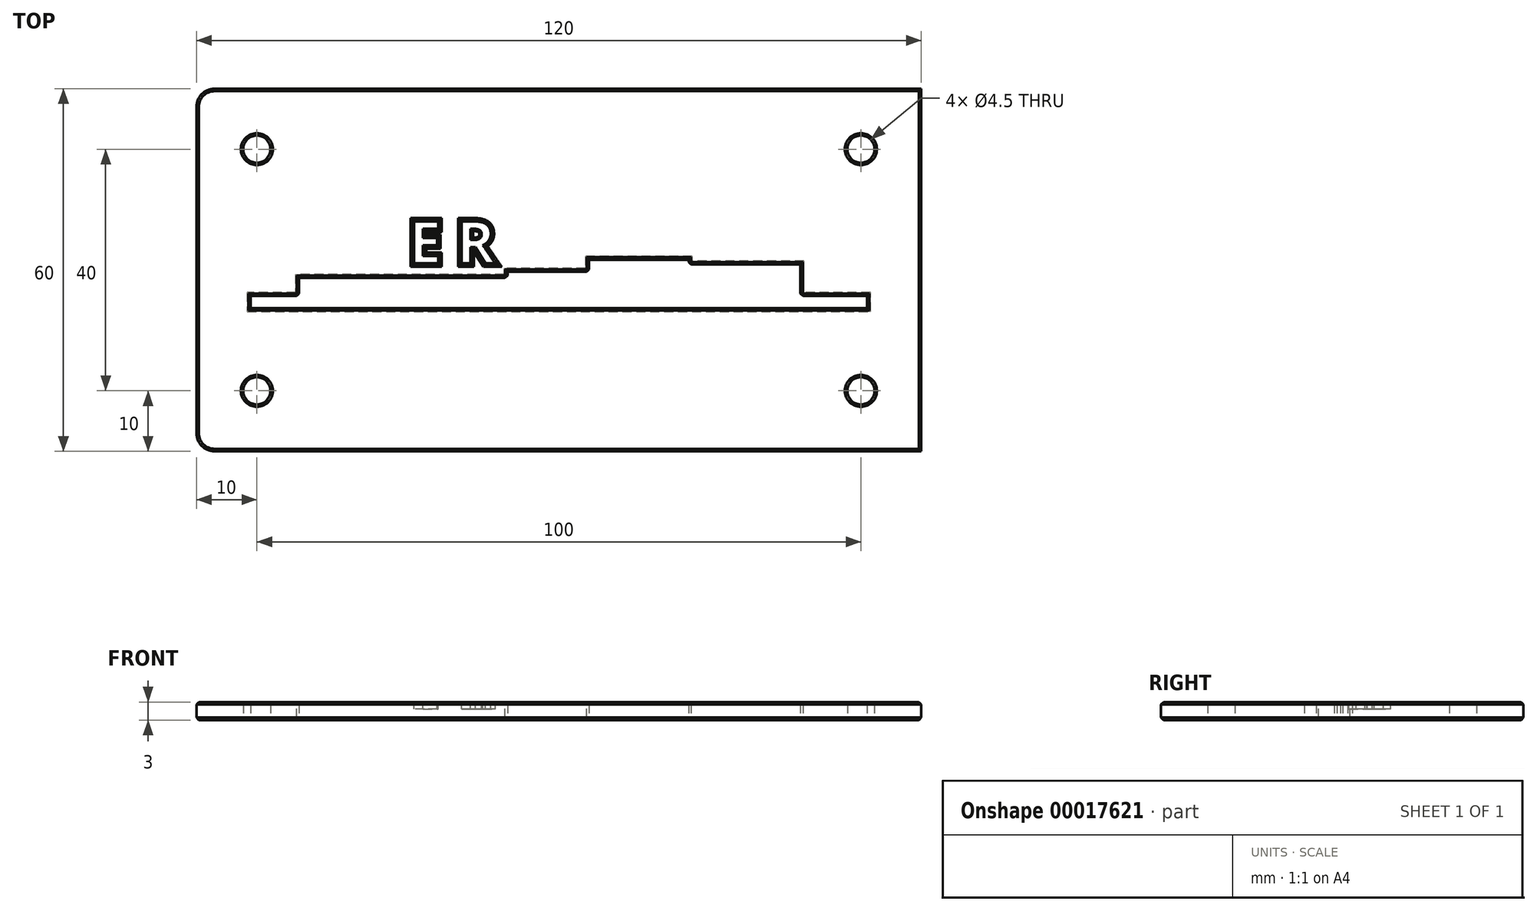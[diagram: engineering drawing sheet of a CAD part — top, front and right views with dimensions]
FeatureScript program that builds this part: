
annotation { "Feature Type Name" : "Feature", "Feature Type Description" : "" }
export const myFeature = defineFeature(function(context is Context, id is Id, definition is map)
    precondition{}
    {
        {
            var Q0;
            Q0=qCreatedBy(makeId("Top.planeOp"),FACE);
            var sketch = newSketch(context, id + "F0", { "sketchPlane" : qUnion([Q0])});
            skLineSegment(sketch, "E0.rect.bottom", {"start": v(-52.5, -30) * mm, "end": v(60, -30) * mm});
            skLineSegment(sketch, "E0.rect.top", {"start": v(-55, 30) * mm, "end": v(60, 30) * mm});
            skLineSegment(sketch, "E0.rect.left", {"start": v(-60, -22.5) * mm, "end": v(-60, 20) * mm});
            skLineSegment(sketch, "E0.rect.right", {"start": v(60, -30) * mm, "end": v(60, 30) * mm});
            skPoint(sketch, "E0.rect.middle", {"position": v(0, 0) * mm});
            skLineSegment(sketch, "E1.left", {"start": v(-60, -30) * mm, "end": v(-60, -22.5) * mm});
            skLineSegment(sketch, "E2.bottom", {"start": v(-60, 30) * mm, "end": v(-55, 30) * mm});
            skLineSegment(sketch, "E2.left", {"start": v(-60, 30) * mm, "end": v(-60, 20) * mm});
            skLineSegment(sketch, "E3.bottom", {"start": v(60, 30) * mm, "end": v(50, 30) * mm});
            skLineSegment(sketch, "E3.left", {"start": v(60, 30) * mm, "end": v(60, 22.5) * mm});
            skLineSegment(sketch, "E4.bottom", {"start": v(60, -30) * mm, "end": v(55, -30) * mm});
            skLineSegment(sketch, "E4.left", {"start": v(60, -30) * mm, "end": v(60, -22.5) * mm});
            skCircle(sketch, "E5", {"center": v(-50, -20) * mm, "radius": 2.25 * mm});
            skCircle(sketch, "E6", {"center": v(-50, 20) * mm, "radius": 2.25 * mm});
            skCircle(sketch, "E7", {"center": v(50, 20) * mm, "radius": 2.25 * mm});
            skCircle(sketch, "E8", {"center": v(50, -20) * mm, "radius": 2.25 * mm});
            skLineSegment(sketch, "E9", {"start": v(-51, 6.3) * mm, "end": v(1.5, 6.3) * mm});
            skLineSegment(sketch, "E10.top", {"start": v(-51, 4.3) * mm, "end": v(-43, 4.3) * mm});
            skLineSegment(sketch, "E10.left", {"start": v(-51, 6.3) * mm, "end": v(-51, 4.3) * mm});
            skLineSegment(sketch, "E10.right", {"start": v(51, 6.3) * mm, "end": v(51, 4.3) * mm});
            skLineSegment(sketch, "E11.top", {"start": v(-43, 1.3) * mm, "end": v(-8.5, 1.3) * mm});
            skLineSegment(sketch, "E11.left", {"start": v(-43, 4.3) * mm, "end": v(-43, 1.3) * mm});
            skLineSegment(sketch, "E12.trimOffspring", {"start": v(43, 4.3) * mm, "end": v(51, 4.3) * mm});
            skLineSegment(sketch, "E13.right", {"start": v(-8.5, 1.3) * mm, "end": v(-8.5, 0.3) * mm});
            skLineSegment(sketch, "E14.left", {"start": v(-8.5, 0.3) * mm, "end": v(-8.5, 1.3) * mm});
            skLineSegment(sketch, "E15.top", {"start": v(-8.5, 0.3) * mm, "end": v(1.5, 0.3) * mm});
            skLineSegment(sketch, "E16", {"start": v(-60, -30) * mm, "end": v(-52.5, -30) * mm});
            skLineSegment(sketch, "E17.right", {"start": v(21.5, 1.3) * mm, "end": v(21.5, 1.6) * mm});
            skLineSegment(sketch, "E18.top", {"start": v(5, -1.7) * mm, "end": v(21.5, -1.7) * mm});
            skLineSegment(sketch, "E18.right", {"start": v(21.5, -0.9) * mm, "end": v(21.5, -1.7) * mm});
            skLineSegment(sketch, "E19.trimOffspring", {"start": v(5, 6.3) * mm, "end": v(21.5, 6.3) * mm});
            skLineSegment(sketch, "E20.trimOffspring", {"start": v(25, 6.3) * mm, "end": v(51, 6.3) * mm});
            skLineSegment(sketch, "E21", {"start": v(-43, 4.3) * mm, "end": v(5, 4.3) * mm, "construction": true});
            skLineSegment(sketch, "E22", {"start": v(1.5, 6.3) * mm, "end": v(5, 6.3) * mm});
            skLineSegment(sketch, "E23", {"start": v(21.5, 6.3) * mm, "end": v(25, 6.3) * mm});
            skLineSegment(sketch, "E24.bottom", {"start": v(43, 4.3) * mm, "end": v(40, 4.3) * mm});
            skLineSegment(sketch, "E24.right", {"start": v(40, 4.3) * mm, "end": v(40, 1.6) * mm});
            skPoint(sketch, "E25.oppositeSnap0", {"position": v(25, 1.6) * mm});
            skPoint(sketch, "E26.orphan", {"position": v(43, -10) * mm});
            skLineSegment(sketch, "E27.trimOffspring", {"start": v(40, 4.3) * mm, "end": v(43, 4.3) * mm, "construction": true});
            skPoint(sketch, "E28.orphan", {"position": v(25, -10.7) * mm});
            skPoint(sketch, "E29.right.start.orphan", {"position": v(25, 13.9) * mm});
            skPoint(sketch, "E30.end.orphan", {"position": v(23, 3.6) * mm});
            skLineSegment(sketch, "E31.top", {"start": v(4.98, 0.3) * mm, "end": v(1.5, 0.3) * mm});
            skLineSegment(sketch, "E32", {"start": v(4.98, 0.3) * mm, "end": v(5, -1.7) * mm});
            skLineSegment(sketch, "E33.top", {"start": v(21.5, -0.9) * mm, "end": v(40, -0.9) * mm});
            skLineSegment(sketch, "E33.right", {"start": v(40, 1.6) * mm, "end": v(40, -0.9) * mm});
            skPoint(sketch, "E34.start.orphan", {"position": v(23, 1.6) * mm});
            skSolve(sketch);
        }
        {
            var Q0;
            Q0=makeQuery(id+"F0.imprint","IMPRINT",FACE,{"disambiguationData":[TD([[makeQuery(id+"F0.imprint","IMPRINT",EDGE,{"derivedFrom":sQuery(id+"F0.wireOp",EDGE,"E0.rect.bottom")}),1.0]])]});
            extrude(context, id + "F1", {"entities" : qUnion([Q0]), "oppositeDirection" : true, "depth" : 3 * mm});
        }
        {
            var Q0;
            Q0=makeQuery(id+"F1.opExtrude","SWEPT_EDGE",EDGE,{"disambiguationData":[OSD([sQuery(id+"F0.wireOp",EDGE,"E4.bottom"),sQuery(id+"F0.wireOp",EDGE,"E4.left")])]});
            var Q1;
            Q1=makeQuery(id+"F1.opExtrude","SWEPT_EDGE",EDGE,{"disambiguationData":[OSD([sQuery(id+"F0.wireOp",EDGE,"E1.bottom"),sQuery(id+"F0.wireOp",EDGE,"E1.left")])]});
            var Q2;
            Q2=makeQuery(id+"F1.opExtrude","SWEPT_EDGE",EDGE,{"disambiguationData":[OSD([sQuery(id+"F0.wireOp",EDGE,"E3.bottom"),sQuery(id+"F0.wireOp",EDGE,"E3.left")])]});
            var Q3;
            Q3=makeQuery(id+"F1.opExtrude","SWEPT_EDGE",EDGE,{"disambiguationData":[OSD([sQuery(id+"F0.wireOp",EDGE,"E2.bottom"),sQuery(id+"F0.wireOp",EDGE,"E2.left")])]});
            fillet(context, id + "F2", {"entities" : qUnion([Q0, Q1, Q2, Q3]), "radius" : 3 * mm, "tangentPropagation" : true, "allowEdgeOverflow" : false});
        }
        {
            var Q0;
            Q0=makeQuery(id+"F1.opExtrude","CAP_FACE",FACE,{"disambiguationData":[OSD([sQuery(id+"F0.wireOp",EDGE,"E0.rect.bottom"),sQuery(id+"F0.wireOp",EDGE,"E0.rect.top"),sQuery(id+"F0.wireOp",EDGE,"E0.rect.left"),sQuery(id+"F0.wireOp",EDGE,"E0.rect.right"),sQuery(id+"F0.wireOp",EDGE,"E1.bottom"),sQuery(id+"F0.wireOp",EDGE,"E1.left"),sQuery(id+"F0.wireOp",EDGE,"E2.bottom"),sQuery(id+"F0.wireOp",EDGE,"E2.left"),sQuery(id+"F0.wireOp",EDGE,"E3.bottom"),sQuery(id+"F0.wireOp",EDGE,"E3.left"),sQuery(id+"F0.wireOp",EDGE,"E4.bottom"),sQuery(id+"F0.wireOp",EDGE,"E4.left"),sQuery(id+"F0.wireOp",EDGE,"E5"),sQuery(id+"F0.wireOp",EDGE,"E6"),sQuery(id+"F0.wireOp",EDGE,"E7"),sQuery(id+"F0.wireOp",EDGE,"E8"),sQuery(id+"F0.wireOp",EDGE,"E9"),sQuery(id+"F0.wireOp",EDGE,"E10.top"),sQuery(id+"F0.wireOp",EDGE,"E10.left"),sQuery(id+"F0.wireOp",EDGE,"E10.right"),sQuery(id+"F0.wireOp",EDGE,"E11.left"),sQuery(id+"F0.wireOp",EDGE,"E11.right"),sQuery(id+"F0.wireOp",EDGE,"E12.trimOffspring"),sQuery(id+"F0.wireOp",EDGE,"E11.top"),sQuery(id+"F0.wireOp",EDGE,"E14.bottom"),sQuery(id+"F0.wireOp",EDGE,"E14.left"),sQuery(id+"F0.wireOp",EDGE,"E14.right"),sQuery(id+"F0.wireOp",EDGE,"2bbd994b-3e8e-4b0d-a158-f2154df3f7ed.trimOffspring"),sQuery(id+"F0.wireOp",EDGE,"E29.top"),sQuery(id+"F0.wireOp",EDGE,"E29.left"),sQuery(id+"F0.wireOp",EDGE,"E29.right")])],"isStart":false});
            var sketch = newSketch(context, id + "F3", { "sketchPlane" : qUnion([Q0])});
            skText(sketch, "E35", { "text": "E", "fontName": "OpenSans-Bold.ttf"});
            skText(sketch, "E36", { "text": "R", "fontName": "OpenSans-Bold.ttf"});
            skPoint(sketch, "E37.right.start.orphan", {"position": v(-26.9, 1.1) * mm});
            skPoint(sketch, "E38.orphan", {"position": v(-8.9, -0.9) * mm});
            skPoint(sketch, "E37.bottom.end.orphan", {"position": v(-26.9, -0.9) * mm});
            skPoint(sketch, "E37.bottom.start.orphan", {"position": v(-17.9, -0.9) * mm});
            skLineSegment(sketch, "E39", {"start": v(-43, -1.3) * mm, "end": v(-8.5, -1.3) * mm});
            const initialGuessF3  = {"E35": [-0.02483, 0.0011, 1, 0, 0.007], "E36": [-0.01696, 0.0011, 1, 0, 0.007]};
            skSetInitialGuess(sketch, initialGuessF3);
            skSolve(sketch);
        }
        {
            var Q0;
            Q0=makeQuery(id+"F3.imprint","IMPRINT",FACE,{"disambiguationData":[TD([[makeQuery(id+"F3.imprint","IMPRINT",EDGE,{"derivedFrom":sQuery(id+"F3.wireOp",EDGE,"E35.sketch_text.stroke-0")}),-1.0]])]});
            var Q1;
            Q1=makeQuery(id+"F3.imprint","IMPRINT",FACE,{"disambiguationData":[TD([[makeQuery(id+"F3.imprint","IMPRINT",EDGE,{"derivedFrom":sQuery(id+"F3.wireOp",EDGE,"E36.sketch_text.stroke-0")}),-1.0]])]});
            extrude(context, id + "F4", {"entities" : qUnion([Q0, Q1]), "operationType" : NewBodyOperationType.REMOVE, "oppositeDirection" : true, "depth" : 1.2 * mm});
        }
        {
            var Q0;
            Q0=makeQuery(id+"F4.boolean.opBoolean","COPY",EDGE,{"derivedFrom":makeQuery(id+"F4.opExtrude","CAP_EDGE",EDGE,{"disambiguationData":[OSD([sQuery(id+"F3.wireOp",EDGE,"E35.sketch_text.stroke-1")])],"isStart":true})});
            var Q1;
            Q1=makeQuery(id+"F4.boolean.opBoolean","COPY",EDGE,{"derivedFrom":makeQuery(id+"F4.opExtrude","CAP_EDGE",EDGE,{"disambiguationData":[OSD([sQuery(id+"F3.wireOp",EDGE,"E35.sketch_text.stroke-2")])],"isStart":true})});
            var Q2;
            Q2=makeQuery(id+"F4.boolean.opBoolean","COPY",EDGE,{"derivedFrom":makeQuery(id+"F4.opExtrude","CAP_EDGE",EDGE,{"disambiguationData":[OSD([sQuery(id+"F3.wireOp",EDGE,"E35.sketch_text.stroke-3")])],"isStart":true})});
            var Q3;
            Q3=makeQuery(id+"F4.boolean.opBoolean","COPY",EDGE,{"derivedFrom":makeQuery(id+"F4.opExtrude","CAP_EDGE",EDGE,{"disambiguationData":[OSD([sQuery(id+"F3.wireOp",EDGE,"E35.sketch_text.stroke-4")])],"isStart":true})});
            var Q4;
            Q4=makeQuery(id+"F4.boolean.opBoolean","COPY",EDGE,{"derivedFrom":makeQuery(id+"F4.opExtrude","CAP_EDGE",EDGE,{"disambiguationData":[OSD([sQuery(id+"F3.wireOp",EDGE,"E35.sketch_text.stroke-5")])],"isStart":true})});
            var Q5;
            Q5=makeQuery(id+"F4.boolean.opBoolean","COPY",EDGE,{"derivedFrom":makeQuery(id+"F4.opExtrude","CAP_EDGE",EDGE,{"disambiguationData":[OSD([sQuery(id+"F3.wireOp",EDGE,"E35.sketch_text.stroke-6")])],"isStart":true})});
            var Q6;
            Q6=makeQuery(id+"F4.boolean.opBoolean","COPY",EDGE,{"derivedFrom":makeQuery(id+"F4.opExtrude","CAP_EDGE",EDGE,{"disambiguationData":[OSD([sQuery(id+"F3.wireOp",EDGE,"E35.sketch_text.stroke-7")])],"isStart":true})});
            var Q7;
            Q7=makeQuery(id+"F4.boolean.opBoolean","COPY",EDGE,{"derivedFrom":makeQuery(id+"F4.opExtrude","CAP_EDGE",EDGE,{"disambiguationData":[OSD([sQuery(id+"F3.wireOp",EDGE,"E35.sketch_text.stroke-8")])],"isStart":true})});
            var Q8;
            Q8=makeQuery(id+"F4.boolean.opBoolean","COPY",EDGE,{"derivedFrom":makeQuery(id+"F4.opExtrude","CAP_EDGE",EDGE,{"disambiguationData":[OSD([sQuery(id+"F3.wireOp",EDGE,"E35.sketch_text.stroke-9")])],"isStart":true})});
            var Q9;
            Q9=makeQuery(id+"F4.boolean.opBoolean","COPY",EDGE,{"derivedFrom":makeQuery(id+"F4.opExtrude","CAP_EDGE",EDGE,{"disambiguationData":[OSD([sQuery(id+"F3.wireOp",EDGE,"E35.sketch_text.stroke-10")])],"isStart":true})});
            var Q10;
            Q10=makeQuery(id+"F4.boolean.opBoolean","COPY",EDGE,{"derivedFrom":makeQuery(id+"F4.opExtrude","CAP_EDGE",EDGE,{"disambiguationData":[OSD([sQuery(id+"F3.wireOp",EDGE,"E35.sketch_text.stroke-11")])],"isStart":true})});
            var Q11;
            Q11=makeQuery(id+"F4.boolean.opBoolean","COPY",EDGE,{"derivedFrom":makeQuery(id+"F4.opExtrude","CAP_EDGE",EDGE,{"disambiguationData":[OSD([sQuery(id+"F3.wireOp",EDGE,"E35.sketch_text.stroke-0")])],"isStart":true})});
            var Q12;
            Q12=makeQuery(id+"F4.boolean.opBoolean","COPY",EDGE,{"derivedFrom":makeQuery(id+"F4.opExtrude","CAP_EDGE",EDGE,{"disambiguationData":[OSD([sQuery(id+"F3.wireOp",EDGE,"E36.sketch_text.stroke-9")])],"isStart":true})});
            var Q13;
            Q13=makeQuery(id+"F4.boolean.opBoolean","COPY",EDGE,{"derivedFrom":makeQuery(id+"F4.opExtrude","CAP_EDGE",EDGE,{"disambiguationData":[OSD([sQuery(id+"F3.wireOp",EDGE,"E36.sketch_text.stroke-8")])],"isStart":true})});
            var Q14;
            Q14=makeQuery(id+"F4.boolean.opBoolean","COPY",EDGE,{"derivedFrom":makeQuery(id+"F4.opExtrude","CAP_EDGE",EDGE,{"disambiguationData":[OSD([sQuery(id+"F3.wireOp",EDGE,"E36.sketch_text.stroke-7")])],"isStart":true})});
            var Q15;
            Q15=makeQuery(id+"F4.boolean.opBoolean","COPY",EDGE,{"derivedFrom":makeQuery(id+"F4.opExtrude","CAP_EDGE",EDGE,{"disambiguationData":[OSD([sQuery(id+"F3.wireOp",EDGE,"E36.sketch_text.stroke-18")])],"isStart":true})});
            var Q16;
            Q16=makeQuery(id+"F4.boolean.opBoolean","COPY",EDGE,{"derivedFrom":makeQuery(id+"F4.opExtrude","CAP_EDGE",EDGE,{"disambiguationData":[OSD([sQuery(id+"F3.wireOp",EDGE,"E36.sketch_text.stroke-17")])],"isStart":true})});
            var Q17;
            Q17=makeQuery(id+"F4.boolean.opBoolean","COPY",EDGE,{"derivedFrom":makeQuery(id+"F4.opExtrude","CAP_EDGE",EDGE,{"disambiguationData":[OSD([sQuery(id+"F3.wireOp",EDGE,"E36.sketch_text.stroke-16")])],"isStart":true})});
            var Q18;
            Q18=makeQuery(id+"F4.boolean.opBoolean","COPY",EDGE,{"derivedFrom":makeQuery(id+"F4.opExtrude","CAP_EDGE",EDGE,{"disambiguationData":[OSD([sQuery(id+"F3.wireOp",EDGE,"E36.sketch_text.stroke-15")])],"isStart":true})});
            var Q19;
            Q19=makeQuery(id+"F4.boolean.opBoolean","COPY",EDGE,{"derivedFrom":makeQuery(id+"F4.opExtrude","CAP_EDGE",EDGE,{"disambiguationData":[OSD([sQuery(id+"F3.wireOp",EDGE,"E36.sketch_text.stroke-14")])],"isStart":true})});
            var Q20;
            Q20=makeQuery(id+"F4.boolean.opBoolean","COPY",EDGE,{"derivedFrom":makeQuery(id+"F4.opExtrude","CAP_EDGE",EDGE,{"disambiguationData":[OSD([sQuery(id+"F3.wireOp",EDGE,"E36.sketch_text.stroke-13")])],"isStart":true})});
            var Q21;
            Q21=makeQuery(id+"F4.boolean.opBoolean","COPY",EDGE,{"derivedFrom":makeQuery(id+"F4.opExtrude","CAP_EDGE",EDGE,{"disambiguationData":[OSD([sQuery(id+"F3.wireOp",EDGE,"E36.sketch_text.stroke-12")])],"isStart":true})});
            var Q22;
            Q22=makeQuery(id+"F4.boolean.opBoolean","COPY",EDGE,{"derivedFrom":makeQuery(id+"F4.opExtrude","CAP_EDGE",EDGE,{"disambiguationData":[OSD([sQuery(id+"F3.wireOp",EDGE,"E36.sketch_text.stroke-11")])],"isStart":true})});
            var Q23;
            Q23=makeQuery(id+"F4.boolean.opBoolean","COPY",EDGE,{"derivedFrom":makeQuery(id+"F4.opExtrude","CAP_EDGE",EDGE,{"disambiguationData":[OSD([sQuery(id+"F3.wireOp",EDGE,"E36.sketch_text.stroke-10")])],"isStart":true})});
            var Q24;
            Q24=makeQuery(id+"F4.boolean.opBoolean","SPLIT",FACE,{"disambiguationData":[TD([makeQuery(id+"F4.opExtrude","SWEPT_FACE",FACE,{"disambiguationData":[OSD([sQuery(id+"F3.wireOp",EDGE,"E36.sketch_text.stroke-0")])]})])],"derivedFrom":makeQuery(id+"F1.opExtrude","CAP_FACE",FACE,{"disambiguationData":[OSD([sQuery(id+"F0.wireOp",EDGE,"E0.rect.bottom"),sQuery(id+"F0.wireOp",EDGE,"E0.rect.top"),sQuery(id+"F0.wireOp",EDGE,"E0.rect.left"),sQuery(id+"F0.wireOp",EDGE,"E0.rect.right"),sQuery(id+"F0.wireOp",EDGE,"E1.left"),sQuery(id+"F0.wireOp",EDGE,"E2.bottom"),sQuery(id+"F0.wireOp",EDGE,"E2.left"),sQuery(id+"F0.wireOp",EDGE,"E3.bottom"),sQuery(id+"F0.wireOp",EDGE,"E3.left"),sQuery(id+"F0.wireOp",EDGE,"E4.bottom"),sQuery(id+"F0.wireOp",EDGE,"E4.left"),sQuery(id+"F0.wireOp",EDGE,"E5"),sQuery(id+"F0.wireOp",EDGE,"E6"),sQuery(id+"F0.wireOp",EDGE,"E7"),sQuery(id+"F0.wireOp",EDGE,"E8"),sQuery(id+"F0.wireOp",EDGE,"E9"),sQuery(id+"F0.wireOp",EDGE,"E10.top"),sQuery(id+"F0.wireOp",EDGE,"E10.left"),sQuery(id+"F0.wireOp",EDGE,"E10.right"),sQuery(id+"F0.wireOp",EDGE,"E11.left"),sQuery(id+"F0.wireOp",EDGE,"E11.right"),sQuery(id+"F0.wireOp",EDGE,"E12.trimOffspring"),sQuery(id+"F0.wireOp",EDGE,"E11.top"),sQuery(id+"F0.wireOp",EDGE,"E29.top"),sQuery(id+"F0.wireOp",EDGE,"E29.left"),sQuery(id+"F0.wireOp",EDGE,"E29.right"),sQuery(id+"F0.wireOp",EDGE,"E15.top"),sQuery(id+"F0.wireOp",EDGE,"E13.right"),sQuery(id+"F0.wireOp",EDGE,"E15.right"),sQuery(id+"F0.wireOp",EDGE,"E16"),sQuery(id+"F0.wireOp",EDGE,"E17.left"),sQuery(id+"F0.wireOp",EDGE,"E17.right"),sQuery(id+"F0.wireOp",EDGE,"b61ca566-ba07-4bff-9836-ffdb72489c4c.left"),sQuery(id+"F0.wireOp",EDGE,"b61ca566-ba07-4bff-9836-ffdb72489c4c.right"),sQuery(id+"F0.wireOp",EDGE,"E18.top"),sQuery(id+"F0.wireOp",EDGE,"E18.left"),sQuery(id+"F0.wireOp",EDGE,"E18.right"),sQuery(id+"F0.wireOp",EDGE,"E19.trimOffspring"),sQuery(id+"F0.wireOp",EDGE,"E20.trimOffspring"),sQuery(id+"F0.wireOp",EDGE,"54661143-fa5e-42c1-9d10-70f3552f3fbd"),sQuery(id+"F0.wireOp",EDGE,"E30"),sQuery(id+"F0.wireOp",EDGE,"E22"),sQuery(id+"F0.wireOp",EDGE,"E23")])],"isStart":false})});
            chamfer(context, id + "F5", {"entities" : qUnion([Q0, Q1, Q2, Q3, Q4, Q5, Q6, Q7, Q8, Q9, Q10, Q11, Q12, Q13, Q14, Q15, Q16, Q17, Q18, Q19, Q20, Q21, Q22, Q23, Q24]), "width" : .4 * mm});
        }
        {
            var Q0;
            Q0=makeQuery(id+"F1.opExtrude","CAP_EDGE",EDGE,{"disambiguationData":[OSD([sQuery(id+"F0.wireOp",EDGE,"E0.rect.bottom"),sQuery(id+"F0.wireOp",EDGE,"E4.bottom"),sQuery(id+"F0.wireOp",EDGE,"E16")])],"isStart":false});
            var Q1;
            {var subQ0=sQuery(id+"F0.wireOp",EDGE,"E1.left");var subQ1=sQuery(id+"F0.wireOp",EDGE,"E16");Q1=makeQuery(id+"F2.opFillet","BLEND_EDGE",EDGE,{"blendedFrom":[makeQuery(id+"F1.opExtrude","SWEPT_EDGE",EDGE,{"disambiguationData":[OSD([subQ0,subQ1])]}),makeQuery(id+"F1.opExtrude","CAP_FACE",FACE,{"disambiguationData":[OSD([sQuery(id+"F0.wireOp",EDGE,"E0.rect.bottom"),sQuery(id+"F0.wireOp",EDGE,"E0.rect.top"),sQuery(id+"F0.wireOp",EDGE,"E0.rect.left"),sQuery(id+"F0.wireOp",EDGE,"E0.rect.right"),subQ0,sQuery(id+"F0.wireOp",EDGE,"E2.bottom"),sQuery(id+"F0.wireOp",EDGE,"E2.left"),sQuery(id+"F0.wireOp",EDGE,"E3.bottom"),sQuery(id+"F0.wireOp",EDGE,"E3.left"),sQuery(id+"F0.wireOp",EDGE,"E4.bottom"),sQuery(id+"F0.wireOp",EDGE,"E4.left"),sQuery(id+"F0.wireOp",EDGE,"E5"),sQuery(id+"F0.wireOp",EDGE,"E6"),sQuery(id+"F0.wireOp",EDGE,"E7"),sQuery(id+"F0.wireOp",EDGE,"E8"),sQuery(id+"F0.wireOp",EDGE,"E9"),sQuery(id+"F0.wireOp",EDGE,"E10.top"),sQuery(id+"F0.wireOp",EDGE,"E10.left"),sQuery(id+"F0.wireOp",EDGE,"E10.right"),sQuery(id+"F0.wireOp",EDGE,"E11.left"),sQuery(id+"F0.wireOp",EDGE,"E11.right"),sQuery(id+"F0.wireOp",EDGE,"E12.trimOffspring"),sQuery(id+"F0.wireOp",EDGE,"E11.top"),sQuery(id+"F0.wireOp",EDGE,"E29.top"),sQuery(id+"F0.wireOp",EDGE,"E29.left"),sQuery(id+"F0.wireOp",EDGE,"E29.right"),sQuery(id+"F0.wireOp",EDGE,"E15.top"),sQuery(id+"F0.wireOp",EDGE,"E13.right"),sQuery(id+"F0.wireOp",EDGE,"E15.right"),subQ1,sQuery(id+"F0.wireOp",EDGE,"E17.left"),sQuery(id+"F0.wireOp",EDGE,"E17.right"),sQuery(id+"F0.wireOp",EDGE,"b61ca566-ba07-4bff-9836-ffdb72489c4c.left"),sQuery(id+"F0.wireOp",EDGE,"b61ca566-ba07-4bff-9836-ffdb72489c4c.right"),sQuery(id+"F0.wireOp",EDGE,"E18.top"),sQuery(id+"F0.wireOp",EDGE,"E18.left"),sQuery(id+"F0.wireOp",EDGE,"E18.right"),sQuery(id+"F0.wireOp",EDGE,"E19.trimOffspring"),sQuery(id+"F0.wireOp",EDGE,"E20.trimOffspring"),sQuery(id+"F0.wireOp",EDGE,"54661143-fa5e-42c1-9d10-70f3552f3fbd"),sQuery(id+"F0.wireOp",EDGE,"E30"),sQuery(id+"F0.wireOp",EDGE,"E22"),sQuery(id+"F0.wireOp",EDGE,"E23")])],"isStart":false})],"blendedInto":[makeQuery(id+"F1.opExtrude","CAP_FACE",FACE,{"disambiguationData":[OSD([sQuery(id+"F0.wireOp",EDGE,"E0.rect.bottom"),sQuery(id+"F0.wireOp",EDGE,"E0.rect.top"),sQuery(id+"F0.wireOp",EDGE,"E0.rect.left"),sQuery(id+"F0.wireOp",EDGE,"E0.rect.right"),subQ0,sQuery(id+"F0.wireOp",EDGE,"E2.bottom"),sQuery(id+"F0.wireOp",EDGE,"E2.left"),sQuery(id+"F0.wireOp",EDGE,"E3.bottom"),sQuery(id+"F0.wireOp",EDGE,"E3.left"),sQuery(id+"F0.wireOp",EDGE,"E4.bottom"),sQuery(id+"F0.wireOp",EDGE,"E4.left"),sQuery(id+"F0.wireOp",EDGE,"E5"),sQuery(id+"F0.wireOp",EDGE,"E6"),sQuery(id+"F0.wireOp",EDGE,"E7"),sQuery(id+"F0.wireOp",EDGE,"E8"),sQuery(id+"F0.wireOp",EDGE,"E9"),sQuery(id+"F0.wireOp",EDGE,"E10.top"),sQuery(id+"F0.wireOp",EDGE,"E10.left"),sQuery(id+"F0.wireOp",EDGE,"E10.right"),sQuery(id+"F0.wireOp",EDGE,"E11.left"),sQuery(id+"F0.wireOp",EDGE,"E11.right"),sQuery(id+"F0.wireOp",EDGE,"E12.trimOffspring"),sQuery(id+"F0.wireOp",EDGE,"E11.top"),sQuery(id+"F0.wireOp",EDGE,"E29.top"),sQuery(id+"F0.wireOp",EDGE,"E29.left"),sQuery(id+"F0.wireOp",EDGE,"E29.right"),sQuery(id+"F0.wireOp",EDGE,"E15.top"),sQuery(id+"F0.wireOp",EDGE,"E13.right"),sQuery(id+"F0.wireOp",EDGE,"E15.right"),subQ1,sQuery(id+"F0.wireOp",EDGE,"E17.left"),sQuery(id+"F0.wireOp",EDGE,"E17.right"),sQuery(id+"F0.wireOp",EDGE,"b61ca566-ba07-4bff-9836-ffdb72489c4c.left"),sQuery(id+"F0.wireOp",EDGE,"b61ca566-ba07-4bff-9836-ffdb72489c4c.right"),sQuery(id+"F0.wireOp",EDGE,"E18.top"),sQuery(id+"F0.wireOp",EDGE,"E18.left"),sQuery(id+"F0.wireOp",EDGE,"E18.right"),sQuery(id+"F0.wireOp",EDGE,"E19.trimOffspring"),sQuery(id+"F0.wireOp",EDGE,"E20.trimOffspring"),sQuery(id+"F0.wireOp",EDGE,"54661143-fa5e-42c1-9d10-70f3552f3fbd"),sQuery(id+"F0.wireOp",EDGE,"E30"),sQuery(id+"F0.wireOp",EDGE,"E22"),sQuery(id+"F0.wireOp",EDGE,"E23")])],"isStart":false})]});}
            var Q2;
            Q2=makeQuery(id+"F1.opExtrude","CAP_EDGE",EDGE,{"disambiguationData":[OSD([sQuery(id+"F0.wireOp",EDGE,"E0.rect.left"),sQuery(id+"F0.wireOp",EDGE,"E1.left"),sQuery(id+"F0.wireOp",EDGE,"E2.left")])],"isStart":false});
            var Q3;
            {var subQ0=sQuery(id+"F0.wireOp",EDGE,"E4.bottom");var subQ1=sQuery(id+"F0.wireOp",EDGE,"E4.left");Q3=makeQuery(id+"F2.opFillet","BLEND_EDGE",EDGE,{"blendedFrom":[makeQuery(id+"F1.opExtrude","SWEPT_EDGE",EDGE,{"disambiguationData":[OSD([subQ0,subQ1])]}),makeQuery(id+"F1.opExtrude","CAP_FACE",FACE,{"disambiguationData":[OSD([sQuery(id+"F0.wireOp",EDGE,"E0.rect.bottom"),sQuery(id+"F0.wireOp",EDGE,"E0.rect.top"),sQuery(id+"F0.wireOp",EDGE,"E0.rect.left"),sQuery(id+"F0.wireOp",EDGE,"E0.rect.right"),sQuery(id+"F0.wireOp",EDGE,"E1.left"),sQuery(id+"F0.wireOp",EDGE,"E2.bottom"),sQuery(id+"F0.wireOp",EDGE,"E2.left"),sQuery(id+"F0.wireOp",EDGE,"E3.bottom"),sQuery(id+"F0.wireOp",EDGE,"E3.left"),subQ0,subQ1,sQuery(id+"F0.wireOp",EDGE,"E5"),sQuery(id+"F0.wireOp",EDGE,"E6"),sQuery(id+"F0.wireOp",EDGE,"E7"),sQuery(id+"F0.wireOp",EDGE,"E8"),sQuery(id+"F0.wireOp",EDGE,"E9"),sQuery(id+"F0.wireOp",EDGE,"E10.top"),sQuery(id+"F0.wireOp",EDGE,"E10.left"),sQuery(id+"F0.wireOp",EDGE,"E10.right"),sQuery(id+"F0.wireOp",EDGE,"E11.left"),sQuery(id+"F0.wireOp",EDGE,"E11.right"),sQuery(id+"F0.wireOp",EDGE,"E12.trimOffspring"),sQuery(id+"F0.wireOp",EDGE,"E11.top"),sQuery(id+"F0.wireOp",EDGE,"E29.top"),sQuery(id+"F0.wireOp",EDGE,"E29.left"),sQuery(id+"F0.wireOp",EDGE,"E29.right"),sQuery(id+"F0.wireOp",EDGE,"E15.top"),sQuery(id+"F0.wireOp",EDGE,"E13.right"),sQuery(id+"F0.wireOp",EDGE,"E15.right"),sQuery(id+"F0.wireOp",EDGE,"E16"),sQuery(id+"F0.wireOp",EDGE,"E17.left"),sQuery(id+"F0.wireOp",EDGE,"E17.right"),sQuery(id+"F0.wireOp",EDGE,"b61ca566-ba07-4bff-9836-ffdb72489c4c.left"),sQuery(id+"F0.wireOp",EDGE,"b61ca566-ba07-4bff-9836-ffdb72489c4c.right"),sQuery(id+"F0.wireOp",EDGE,"E18.top"),sQuery(id+"F0.wireOp",EDGE,"E18.left"),sQuery(id+"F0.wireOp",EDGE,"E18.right"),sQuery(id+"F0.wireOp",EDGE,"E19.trimOffspring"),sQuery(id+"F0.wireOp",EDGE,"E20.trimOffspring"),sQuery(id+"F0.wireOp",EDGE,"54661143-fa5e-42c1-9d10-70f3552f3fbd"),sQuery(id+"F0.wireOp",EDGE,"E30"),sQuery(id+"F0.wireOp",EDGE,"E22"),sQuery(id+"F0.wireOp",EDGE,"E23")])],"isStart":false})],"blendedInto":[makeQuery(id+"F1.opExtrude","CAP_FACE",FACE,{"disambiguationData":[OSD([sQuery(id+"F0.wireOp",EDGE,"E0.rect.bottom"),sQuery(id+"F0.wireOp",EDGE,"E0.rect.top"),sQuery(id+"F0.wireOp",EDGE,"E0.rect.left"),sQuery(id+"F0.wireOp",EDGE,"E0.rect.right"),sQuery(id+"F0.wireOp",EDGE,"E1.left"),sQuery(id+"F0.wireOp",EDGE,"E2.bottom"),sQuery(id+"F0.wireOp",EDGE,"E2.left"),sQuery(id+"F0.wireOp",EDGE,"E3.bottom"),sQuery(id+"F0.wireOp",EDGE,"E3.left"),subQ0,subQ1,sQuery(id+"F0.wireOp",EDGE,"E5"),sQuery(id+"F0.wireOp",EDGE,"E6"),sQuery(id+"F0.wireOp",EDGE,"E7"),sQuery(id+"F0.wireOp",EDGE,"E8"),sQuery(id+"F0.wireOp",EDGE,"E9"),sQuery(id+"F0.wireOp",EDGE,"E10.top"),sQuery(id+"F0.wireOp",EDGE,"E10.left"),sQuery(id+"F0.wireOp",EDGE,"E10.right"),sQuery(id+"F0.wireOp",EDGE,"E11.left"),sQuery(id+"F0.wireOp",EDGE,"E11.right"),sQuery(id+"F0.wireOp",EDGE,"E12.trimOffspring"),sQuery(id+"F0.wireOp",EDGE,"E11.top"),sQuery(id+"F0.wireOp",EDGE,"E29.top"),sQuery(id+"F0.wireOp",EDGE,"E29.left"),sQuery(id+"F0.wireOp",EDGE,"E29.right"),sQuery(id+"F0.wireOp",EDGE,"E15.top"),sQuery(id+"F0.wireOp",EDGE,"E13.right"),sQuery(id+"F0.wireOp",EDGE,"E15.right"),sQuery(id+"F0.wireOp",EDGE,"E16"),sQuery(id+"F0.wireOp",EDGE,"E17.left"),sQuery(id+"F0.wireOp",EDGE,"E17.right"),sQuery(id+"F0.wireOp",EDGE,"b61ca566-ba07-4bff-9836-ffdb72489c4c.left"),sQuery(id+"F0.wireOp",EDGE,"b61ca566-ba07-4bff-9836-ffdb72489c4c.right"),sQuery(id+"F0.wireOp",EDGE,"E18.top"),sQuery(id+"F0.wireOp",EDGE,"E18.left"),sQuery(id+"F0.wireOp",EDGE,"E18.right"),sQuery(id+"F0.wireOp",EDGE,"E19.trimOffspring"),sQuery(id+"F0.wireOp",EDGE,"E20.trimOffspring"),sQuery(id+"F0.wireOp",EDGE,"54661143-fa5e-42c1-9d10-70f3552f3fbd"),sQuery(id+"F0.wireOp",EDGE,"E30"),sQuery(id+"F0.wireOp",EDGE,"E22"),sQuery(id+"F0.wireOp",EDGE,"E23")])],"isStart":false})]});}
            var Q4;
            Q4=makeQuery(id+"F1.opExtrude","CAP_EDGE",EDGE,{"disambiguationData":[OSD([sQuery(id+"F0.wireOp",EDGE,"E0.rect.right"),sQuery(id+"F0.wireOp",EDGE,"E3.left"),sQuery(id+"F0.wireOp",EDGE,"E4.left")])],"isStart":false});
            var Q5;
            {var subQ0=sQuery(id+"F0.wireOp",EDGE,"E3.bottom");var subQ1=sQuery(id+"F0.wireOp",EDGE,"E3.left");Q5=makeQuery(id+"F2.opFillet","BLEND_EDGE",EDGE,{"blendedFrom":[makeQuery(id+"F1.opExtrude","SWEPT_EDGE",EDGE,{"disambiguationData":[OSD([subQ0,subQ1])]}),makeQuery(id+"F1.opExtrude","CAP_FACE",FACE,{"disambiguationData":[OSD([sQuery(id+"F0.wireOp",EDGE,"E0.rect.bottom"),sQuery(id+"F0.wireOp",EDGE,"E0.rect.top"),sQuery(id+"F0.wireOp",EDGE,"E0.rect.left"),sQuery(id+"F0.wireOp",EDGE,"E0.rect.right"),sQuery(id+"F0.wireOp",EDGE,"E1.left"),sQuery(id+"F0.wireOp",EDGE,"E2.bottom"),sQuery(id+"F0.wireOp",EDGE,"E2.left"),subQ0,subQ1,sQuery(id+"F0.wireOp",EDGE,"E4.bottom"),sQuery(id+"F0.wireOp",EDGE,"E4.left"),sQuery(id+"F0.wireOp",EDGE,"E5"),sQuery(id+"F0.wireOp",EDGE,"E6"),sQuery(id+"F0.wireOp",EDGE,"E7"),sQuery(id+"F0.wireOp",EDGE,"E8"),sQuery(id+"F0.wireOp",EDGE,"E9"),sQuery(id+"F0.wireOp",EDGE,"E10.top"),sQuery(id+"F0.wireOp",EDGE,"E10.left"),sQuery(id+"F0.wireOp",EDGE,"E10.right"),sQuery(id+"F0.wireOp",EDGE,"E11.left"),sQuery(id+"F0.wireOp",EDGE,"E11.right"),sQuery(id+"F0.wireOp",EDGE,"E12.trimOffspring"),sQuery(id+"F0.wireOp",EDGE,"E11.top"),sQuery(id+"F0.wireOp",EDGE,"E29.top"),sQuery(id+"F0.wireOp",EDGE,"E29.left"),sQuery(id+"F0.wireOp",EDGE,"E29.right"),sQuery(id+"F0.wireOp",EDGE,"E15.top"),sQuery(id+"F0.wireOp",EDGE,"E13.right"),sQuery(id+"F0.wireOp",EDGE,"E15.right"),sQuery(id+"F0.wireOp",EDGE,"E16"),sQuery(id+"F0.wireOp",EDGE,"E17.left"),sQuery(id+"F0.wireOp",EDGE,"E17.right"),sQuery(id+"F0.wireOp",EDGE,"b61ca566-ba07-4bff-9836-ffdb72489c4c.left"),sQuery(id+"F0.wireOp",EDGE,"b61ca566-ba07-4bff-9836-ffdb72489c4c.right"),sQuery(id+"F0.wireOp",EDGE,"E18.top"),sQuery(id+"F0.wireOp",EDGE,"E18.left"),sQuery(id+"F0.wireOp",EDGE,"E18.right"),sQuery(id+"F0.wireOp",EDGE,"E19.trimOffspring"),sQuery(id+"F0.wireOp",EDGE,"E20.trimOffspring"),sQuery(id+"F0.wireOp",EDGE,"54661143-fa5e-42c1-9d10-70f3552f3fbd"),sQuery(id+"F0.wireOp",EDGE,"E30"),sQuery(id+"F0.wireOp",EDGE,"E22"),sQuery(id+"F0.wireOp",EDGE,"E23")])],"isStart":false})],"blendedInto":[makeQuery(id+"F1.opExtrude","CAP_FACE",FACE,{"disambiguationData":[OSD([sQuery(id+"F0.wireOp",EDGE,"E0.rect.bottom"),sQuery(id+"F0.wireOp",EDGE,"E0.rect.top"),sQuery(id+"F0.wireOp",EDGE,"E0.rect.left"),sQuery(id+"F0.wireOp",EDGE,"E0.rect.right"),sQuery(id+"F0.wireOp",EDGE,"E1.left"),sQuery(id+"F0.wireOp",EDGE,"E2.bottom"),sQuery(id+"F0.wireOp",EDGE,"E2.left"),subQ0,subQ1,sQuery(id+"F0.wireOp",EDGE,"E4.bottom"),sQuery(id+"F0.wireOp",EDGE,"E4.left"),sQuery(id+"F0.wireOp",EDGE,"E5"),sQuery(id+"F0.wireOp",EDGE,"E6"),sQuery(id+"F0.wireOp",EDGE,"E7"),sQuery(id+"F0.wireOp",EDGE,"E8"),sQuery(id+"F0.wireOp",EDGE,"E9"),sQuery(id+"F0.wireOp",EDGE,"E10.top"),sQuery(id+"F0.wireOp",EDGE,"E10.left"),sQuery(id+"F0.wireOp",EDGE,"E10.right"),sQuery(id+"F0.wireOp",EDGE,"E11.left"),sQuery(id+"F0.wireOp",EDGE,"E11.right"),sQuery(id+"F0.wireOp",EDGE,"E12.trimOffspring"),sQuery(id+"F0.wireOp",EDGE,"E11.top"),sQuery(id+"F0.wireOp",EDGE,"E29.top"),sQuery(id+"F0.wireOp",EDGE,"E29.left"),sQuery(id+"F0.wireOp",EDGE,"E29.right"),sQuery(id+"F0.wireOp",EDGE,"E15.top"),sQuery(id+"F0.wireOp",EDGE,"E13.right"),sQuery(id+"F0.wireOp",EDGE,"E15.right"),sQuery(id+"F0.wireOp",EDGE,"E16"),sQuery(id+"F0.wireOp",EDGE,"E17.left"),sQuery(id+"F0.wireOp",EDGE,"E17.right"),sQuery(id+"F0.wireOp",EDGE,"b61ca566-ba07-4bff-9836-ffdb72489c4c.left"),sQuery(id+"F0.wireOp",EDGE,"b61ca566-ba07-4bff-9836-ffdb72489c4c.right"),sQuery(id+"F0.wireOp",EDGE,"E18.top"),sQuery(id+"F0.wireOp",EDGE,"E18.left"),sQuery(id+"F0.wireOp",EDGE,"E18.right"),sQuery(id+"F0.wireOp",EDGE,"E19.trimOffspring"),sQuery(id+"F0.wireOp",EDGE,"E20.trimOffspring"),sQuery(id+"F0.wireOp",EDGE,"54661143-fa5e-42c1-9d10-70f3552f3fbd"),sQuery(id+"F0.wireOp",EDGE,"E30"),sQuery(id+"F0.wireOp",EDGE,"E22"),sQuery(id+"F0.wireOp",EDGE,"E23")])],"isStart":false})]});}
            var Q6;
            Q6=makeQuery(id+"F1.opExtrude","CAP_EDGE",EDGE,{"disambiguationData":[OSD([sQuery(id+"F0.wireOp",EDGE,"E0.rect.top"),sQuery(id+"F0.wireOp",EDGE,"E2.bottom"),sQuery(id+"F0.wireOp",EDGE,"E3.bottom")])],"isStart":false});
            var Q7;
            {var subQ0=sQuery(id+"F0.wireOp",EDGE,"E2.bottom");var subQ1=sQuery(id+"F0.wireOp",EDGE,"E2.left");Q7=makeQuery(id+"F2.opFillet","BLEND_EDGE",EDGE,{"blendedFrom":[makeQuery(id+"F1.opExtrude","SWEPT_EDGE",EDGE,{"disambiguationData":[OSD([subQ0,subQ1])]}),makeQuery(id+"F1.opExtrude","CAP_FACE",FACE,{"disambiguationData":[OSD([sQuery(id+"F0.wireOp",EDGE,"E0.rect.bottom"),sQuery(id+"F0.wireOp",EDGE,"E0.rect.top"),sQuery(id+"F0.wireOp",EDGE,"E0.rect.left"),sQuery(id+"F0.wireOp",EDGE,"E0.rect.right"),sQuery(id+"F0.wireOp",EDGE,"E1.left"),subQ0,subQ1,sQuery(id+"F0.wireOp",EDGE,"E3.bottom"),sQuery(id+"F0.wireOp",EDGE,"E3.left"),sQuery(id+"F0.wireOp",EDGE,"E4.bottom"),sQuery(id+"F0.wireOp",EDGE,"E4.left"),sQuery(id+"F0.wireOp",EDGE,"E5"),sQuery(id+"F0.wireOp",EDGE,"E6"),sQuery(id+"F0.wireOp",EDGE,"E7"),sQuery(id+"F0.wireOp",EDGE,"E8"),sQuery(id+"F0.wireOp",EDGE,"E9"),sQuery(id+"F0.wireOp",EDGE,"E10.top"),sQuery(id+"F0.wireOp",EDGE,"E10.left"),sQuery(id+"F0.wireOp",EDGE,"E10.right"),sQuery(id+"F0.wireOp",EDGE,"E11.left"),sQuery(id+"F0.wireOp",EDGE,"E11.right"),sQuery(id+"F0.wireOp",EDGE,"E12.trimOffspring"),sQuery(id+"F0.wireOp",EDGE,"E11.top"),sQuery(id+"F0.wireOp",EDGE,"E29.top"),sQuery(id+"F0.wireOp",EDGE,"E29.left"),sQuery(id+"F0.wireOp",EDGE,"E29.right"),sQuery(id+"F0.wireOp",EDGE,"E15.top"),sQuery(id+"F0.wireOp",EDGE,"E13.right"),sQuery(id+"F0.wireOp",EDGE,"E15.right"),sQuery(id+"F0.wireOp",EDGE,"E16"),sQuery(id+"F0.wireOp",EDGE,"E17.left"),sQuery(id+"F0.wireOp",EDGE,"E17.right"),sQuery(id+"F0.wireOp",EDGE,"b61ca566-ba07-4bff-9836-ffdb72489c4c.left"),sQuery(id+"F0.wireOp",EDGE,"b61ca566-ba07-4bff-9836-ffdb72489c4c.right"),sQuery(id+"F0.wireOp",EDGE,"E18.top"),sQuery(id+"F0.wireOp",EDGE,"E18.left"),sQuery(id+"F0.wireOp",EDGE,"E18.right"),sQuery(id+"F0.wireOp",EDGE,"E19.trimOffspring"),sQuery(id+"F0.wireOp",EDGE,"E20.trimOffspring"),sQuery(id+"F0.wireOp",EDGE,"54661143-fa5e-42c1-9d10-70f3552f3fbd"),sQuery(id+"F0.wireOp",EDGE,"E30"),sQuery(id+"F0.wireOp",EDGE,"E22"),sQuery(id+"F0.wireOp",EDGE,"E23")])],"isStart":false})],"blendedInto":[makeQuery(id+"F1.opExtrude","CAP_FACE",FACE,{"disambiguationData":[OSD([sQuery(id+"F0.wireOp",EDGE,"E0.rect.bottom"),sQuery(id+"F0.wireOp",EDGE,"E0.rect.top"),sQuery(id+"F0.wireOp",EDGE,"E0.rect.left"),sQuery(id+"F0.wireOp",EDGE,"E0.rect.right"),sQuery(id+"F0.wireOp",EDGE,"E1.left"),subQ0,subQ1,sQuery(id+"F0.wireOp",EDGE,"E3.bottom"),sQuery(id+"F0.wireOp",EDGE,"E3.left"),sQuery(id+"F0.wireOp",EDGE,"E4.bottom"),sQuery(id+"F0.wireOp",EDGE,"E4.left"),sQuery(id+"F0.wireOp",EDGE,"E5"),sQuery(id+"F0.wireOp",EDGE,"E6"),sQuery(id+"F0.wireOp",EDGE,"E7"),sQuery(id+"F0.wireOp",EDGE,"E8"),sQuery(id+"F0.wireOp",EDGE,"E9"),sQuery(id+"F0.wireOp",EDGE,"E10.top"),sQuery(id+"F0.wireOp",EDGE,"E10.left"),sQuery(id+"F0.wireOp",EDGE,"E10.right"),sQuery(id+"F0.wireOp",EDGE,"E11.left"),sQuery(id+"F0.wireOp",EDGE,"E11.right"),sQuery(id+"F0.wireOp",EDGE,"E12.trimOffspring"),sQuery(id+"F0.wireOp",EDGE,"E11.top"),sQuery(id+"F0.wireOp",EDGE,"E29.top"),sQuery(id+"F0.wireOp",EDGE,"E29.left"),sQuery(id+"F0.wireOp",EDGE,"E29.right"),sQuery(id+"F0.wireOp",EDGE,"E15.top"),sQuery(id+"F0.wireOp",EDGE,"E13.right"),sQuery(id+"F0.wireOp",EDGE,"E15.right"),sQuery(id+"F0.wireOp",EDGE,"E16"),sQuery(id+"F0.wireOp",EDGE,"E17.left"),sQuery(id+"F0.wireOp",EDGE,"E17.right"),sQuery(id+"F0.wireOp",EDGE,"b61ca566-ba07-4bff-9836-ffdb72489c4c.left"),sQuery(id+"F0.wireOp",EDGE,"b61ca566-ba07-4bff-9836-ffdb72489c4c.right"),sQuery(id+"F0.wireOp",EDGE,"E18.top"),sQuery(id+"F0.wireOp",EDGE,"E18.left"),sQuery(id+"F0.wireOp",EDGE,"E18.right"),sQuery(id+"F0.wireOp",EDGE,"E19.trimOffspring"),sQuery(id+"F0.wireOp",EDGE,"E20.trimOffspring"),sQuery(id+"F0.wireOp",EDGE,"54661143-fa5e-42c1-9d10-70f3552f3fbd"),sQuery(id+"F0.wireOp",EDGE,"E30"),sQuery(id+"F0.wireOp",EDGE,"E22"),sQuery(id+"F0.wireOp",EDGE,"E23")])],"isStart":false})]});}
            var Q8;
            Q8=makeQuery(id+"F1.opExtrude","CAP_EDGE",EDGE,{"disambiguationData":[OSD([sQuery(id+"F0.wireOp",EDGE,"E6")])],"isStart":false});
            var Q9;
            Q9=makeQuery(id+"F1.opExtrude","CAP_EDGE",EDGE,{"disambiguationData":[OSD([sQuery(id+"F0.wireOp",EDGE,"E7")])],"isStart":false});
            var Q10;
            Q10=makeQuery(id+"F1.opExtrude","CAP_EDGE",EDGE,{"disambiguationData":[OSD([sQuery(id+"F0.wireOp",EDGE,"E5")])],"isStart":false});
            var Q11;
            Q11=makeQuery(id+"F1.opExtrude","CAP_EDGE",EDGE,{"disambiguationData":[OSD([sQuery(id+"F0.wireOp",EDGE,"E8")])],"isStart":false});
            var Q12;
            Q12=makeQuery(id+"F1.opExtrude","CAP_EDGE",EDGE,{"disambiguationData":[OSD([sQuery(id+"F0.wireOp",EDGE,"E29.top")])],"isStart":false});
            var Q13;
            Q13=makeQuery(id+"F1.opExtrude","CAP_EDGE",EDGE,{"disambiguationData":[OSD([sQuery(id+"F0.wireOp",EDGE,"E29.right"),sQuery(id+"F0.wireOp",EDGE,"E17.left")])],"isStart":false});
            var Q14;
            Q14=makeQuery(id+"F1.opExtrude","CAP_EDGE",EDGE,{"disambiguationData":[OSD([sQuery(id+"F0.wireOp",EDGE,"E11.right"),sQuery(id+"F0.wireOp",EDGE,"E29.left")])],"isStart":false});
            var Q15;
            Q15=makeQuery(id+"F1.opExtrude","CAP_EDGE",EDGE,{"disambiguationData":[OSD([sQuery(id+"F0.wireOp",EDGE,"E12.trimOffspring")])],"isStart":false});
            var Q16;
            Q16=makeQuery(id+"F1.opExtrude","CAP_EDGE",EDGE,{"disambiguationData":[OSD([sQuery(id+"F0.wireOp",EDGE,"E10.right")])],"isStart":false});
            var Q17;
            Q17=makeQuery(id+"F1.opExtrude","CAP_EDGE",EDGE,{"disambiguationData":[OSD([sQuery(id+"F0.wireOp",EDGE,"E9"),sQuery(id+"F0.wireOp",EDGE,"E19.trimOffspring"),sQuery(id+"F0.wireOp",EDGE,"E20.trimOffspring"),sQuery(id+"F0.wireOp",EDGE,"E22"),sQuery(id+"F0.wireOp",EDGE,"E23")])],"isStart":false});
            var Q18;
            Q18=makeQuery(id+"F1.opExtrude","CAP_EDGE",EDGE,{"disambiguationData":[OSD([sQuery(id+"F0.wireOp",EDGE,"E10.left")])],"isStart":false});
            var Q19;
            Q19=makeQuery(id+"F1.opExtrude","CAP_EDGE",EDGE,{"disambiguationData":[OSD([sQuery(id+"F0.wireOp",EDGE,"E10.top")])],"isStart":false});
            var Q20;
            Q20=makeQuery(id+"F1.opExtrude","CAP_EDGE",EDGE,{"disambiguationData":[OSD([sQuery(id+"F0.wireOp",EDGE,"E11.left")])],"isStart":false});
            var Q21;
            Q21=makeQuery(id+"F1.opExtrude","CAP_EDGE",EDGE,{"disambiguationData":[OSD([sQuery(id+"F0.wireOp",EDGE,"E11.top")])],"isStart":false});
            var Q22;
            Q22=makeQuery(id+"F1.opExtrude","CAP_EDGE",EDGE,{"disambiguationData":[OSD([sQuery(id+"F0.wireOp",EDGE,"E13.right")])],"isStart":false});
            var Q23;
            Q23=makeQuery(id+"F1.opExtrude","CAP_EDGE",EDGE,{"disambiguationData":[OSD([sQuery(id+"F0.wireOp",EDGE,"E15.top")])],"isStart":false});
            var Q24;
            Q24=makeQuery(id+"F1.opExtrude","CAP_EDGE",EDGE,{"disambiguationData":[OSD([sQuery(id+"F0.wireOp",EDGE,"E15.right"),sQuery(id+"F0.wireOp",EDGE,"b61ca566-ba07-4bff-9836-ffdb72489c4c.left")])],"isStart":false});
            var Q25;
            Q25=makeQuery(id+"F1.opExtrude","CAP_EDGE",EDGE,{"disambiguationData":[OSD([sQuery(id+"F0.wireOp",EDGE,"54661143-fa5e-42c1-9d10-70f3552f3fbd")])],"isStart":false});
            var Q26;
            Q26=makeQuery(id+"F1.opExtrude","CAP_EDGE",EDGE,{"disambiguationData":[OSD([sQuery(id+"F0.wireOp",EDGE,"b61ca566-ba07-4bff-9836-ffdb72489c4c.right"),sQuery(id+"F0.wireOp",EDGE,"E18.left")])],"isStart":false});
            var Q27;
            Q27=makeQuery(id+"F1.opExtrude","CAP_EDGE",EDGE,{"disambiguationData":[OSD([sQuery(id+"F0.wireOp",EDGE,"E18.top")])],"isStart":false});
            var Q28;
            Q28=makeQuery(id+"F1.opExtrude","CAP_EDGE",EDGE,{"disambiguationData":[OSD([sQuery(id+"F0.wireOp",EDGE,"E17.right"),sQuery(id+"F0.wireOp",EDGE,"E18.right")])],"isStart":false});
            var Q29;
            Q29=makeQuery(id+"F1.opExtrude","CAP_EDGE",EDGE,{"disambiguationData":[OSD([sQuery(id+"F0.wireOp",EDGE,"E30")])],"isStart":false});
            var Q30;
            Q30=makeQuery(id+"F1.opExtrude","CAP_EDGE",EDGE,{"disambiguationData":[OSD([sQuery(id+"F0.wireOp",EDGE,"E25.top"),sQuery(id+"F0.wireOp",EDGE,"E34")])],"isStart":false});
            var Q31;
            Q31=makeQuery(id+"F1.opExtrude","CAP_EDGE",EDGE,{"disambiguationData":[OSD([sQuery(id+"F0.wireOp",EDGE,"E24.right")])],"isStart":false});
            var Q32;
            Q32=makeQuery(id+"F1.opExtrude","CAP_EDGE",EDGE,{"disambiguationData":[OSD([sQuery(id+"F0.wireOp",EDGE,"E32")])],"isStart":false});
            var Q33;
            {var subQ0=sQuery(id+"F0.wireOp",EDGE,"E24.right");var subQ1=sQuery(id+"F0.wireOp",EDGE,"E34");var subQ2=sQuery(id+"F0.wireOp",EDGE,"E25.top");var subQ3=sQuery(id+"F0.wireOp",EDGE,"E32");var subQ4=sQuery(id+"F0.wireOp",EDGE,"E8");var subQ5=sQuery(id+"F0.wireOp",EDGE,"E3.left");var subQ6=sQuery(id+"F0.wireOp",EDGE,"E3.bottom");var subQ7=sQuery(id+"F0.wireOp",EDGE,"E10.top");var subQ8=sQuery(id+"F0.wireOp",EDGE,"E16");var subQ9=sQuery(id+"F0.wireOp",EDGE,"E1.left");var subQ10=sQuery(id+"F0.wireOp",EDGE,"E2.left");var subQ11=sQuery(id+"F0.wireOp",EDGE,"E2.bottom");var subQ12=sQuery(id+"F0.wireOp",EDGE,"E11.top");var subQ13=sQuery(id+"F0.wireOp",EDGE,"E7");var subQ14=sQuery(id+"F0.wireOp",EDGE,"E6");var subQ15=sQuery(id+"F0.wireOp",EDGE,"E5");var subQ16=sQuery(id+"F0.wireOp",EDGE,"E18.top");var subQ17=sQuery(id+"F0.wireOp",EDGE,"E4.bottom");var subQ18=sQuery(id+"F0.wireOp",EDGE,"E0.rect.bottom");var subQ19=sQuery(id+"F0.wireOp",EDGE,"E0.rect.top");var subQ20=sQuery(id+"F0.wireOp",EDGE,"E10.right");var subQ21=sQuery(id+"F0.wireOp",EDGE,"E4.left");var subQ22=sQuery(id+"F0.wireOp",EDGE,"E13.right");var subQ23=sQuery(id+"F0.wireOp",EDGE,"E23");var subQ24=sQuery(id+"F0.wireOp",EDGE,"E22");var subQ25=sQuery(id+"F0.wireOp",EDGE,"E20.trimOffspring");var subQ26=sQuery(id+"F0.wireOp",EDGE,"E19.trimOffspring");var subQ27=sQuery(id+"F0.wireOp",EDGE,"E9");var subQ28=sQuery(id+"F0.wireOp",EDGE,"E18.right");var subQ29=sQuery(id+"F0.wireOp",EDGE,"E17.right");var subQ30=sQuery(id+"F0.wireOp",EDGE,"E31.top");var subQ31=sQuery(id+"F0.wireOp",EDGE,"E15.top");var subQ32=sQuery(id+"F0.wireOp",EDGE,"E0.rect.left");var subQ33=sQuery(id+"F0.wireOp",EDGE,"E0.rect.right");var subQ34=sQuery(id+"F0.wireOp",EDGE,"E10.left");var subQ35=sQuery(id+"F0.wireOp",EDGE,"E24.bottom");var subQ36=sQuery(id+"F0.wireOp",EDGE,"E12.trimOffspring");var subQ37=sQuery(id+"F0.wireOp",EDGE,"E11.left");Q33=makeQuery(id+"F4.boolean.opBoolean","SPLIT",FACE,{"disambiguationData":[TD([makeQuery(id+"F1.opExtrude","SWEPT_FACE",FACE,{"disambiguationData":[OSD([subQ15])]})])],"derivedFrom":makeQuery(id+"F1.opExtrude","CAP_FACE",FACE,{"disambiguationData":[OSD([subQ18,subQ19,subQ32,subQ33,subQ9,subQ11,subQ10,subQ6,subQ5,subQ17,subQ21,subQ15,subQ14,subQ13,subQ4,subQ27,subQ7,subQ34,subQ20,subQ37,subQ36,subQ12,subQ31,subQ22,subQ8,subQ29,subQ16,subQ28,subQ26,subQ25,subQ24,subQ23,subQ35,subQ2,subQ0,subQ1,subQ30,subQ3])],"isStart":false})});}
            var Q34;
            Q34=makeQuery(id+"F1.opExtrude","SWEPT_EDGE",EDGE,{"disambiguationData":[OSD([sQuery(id+"F0.wireOp",EDGE,"E11.top"),sQuery(id+"F0.wireOp",EDGE,"E13.right")])]});
            var Q35;
            Q35=makeQuery(id+"F1.opExtrude","SWEPT_EDGE",EDGE,{"disambiguationData":[OSD([sQuery(id+"F0.wireOp",EDGE,"E31.top"),sQuery(id+"F0.wireOp",EDGE,"E32")])]});
            var Q36;
            Q36=makeQuery(id+"F1.opExtrude","SWEPT_EDGE",EDGE,{"disambiguationData":[OSD([sQuery(id+"F0.wireOp",EDGE,"E10.top"),sQuery(id+"F0.wireOp",EDGE,"E11.left")])]});
            var Q37;
            Q37=makeQuery(id+"F1.opExtrude","SWEPT_EDGE",EDGE,{"disambiguationData":[OSD([sQuery(id+"F0.wireOp",EDGE,"E17.right"),sQuery(id+"F0.wireOp",EDGE,"E34")])]});
            var Q38;
            Q38=makeQuery(id+"F1.opExtrude","SWEPT_EDGE",EDGE,{"disambiguationData":[OSD([sQuery(id+"F0.wireOp",EDGE,"E24.bottom"),sQuery(id+"F0.wireOp",EDGE,"E24.right")])]});
            var Q39;
            Q39=makeQuery(id+"F1.opExtrude","CAP_EDGE",EDGE,{"disambiguationData":[OSD([sQuery(id+"F0.wireOp",EDGE,"E10.top")])],"isStart":true});
            var Q40;
            Q40=makeQuery(id+"F1.opExtrude","CAP_EDGE",EDGE,{"disambiguationData":[OSD([sQuery(id+"F0.wireOp",EDGE,"E10.left")])],"isStart":true});
            var Q41;
            Q41=makeQuery(id+"F1.opExtrude","CAP_EDGE",EDGE,{"disambiguationData":[OSD([sQuery(id+"F0.wireOp",EDGE,"E11.left")])],"isStart":true});
            var Q42;
            Q42=makeQuery(id+"F1.opExtrude","CAP_EDGE",EDGE,{"disambiguationData":[OSD([sQuery(id+"F0.wireOp",EDGE,"E11.top")])],"isStart":true});
            var Q43;
            Q43=makeQuery(id+"F1.opExtrude","CAP_EDGE",EDGE,{"disambiguationData":[OSD([sQuery(id+"F0.wireOp",EDGE,"E13.right")])],"isStart":true});
            var Q44;
            Q44=makeQuery(id+"F1.opExtrude","CAP_EDGE",EDGE,{"disambiguationData":[OSD([sQuery(id+"F0.wireOp",EDGE,"E15.top"),sQuery(id+"F0.wireOp",EDGE,"E31.top")])],"isStart":true});
            var Q45;
            Q45=makeQuery(id+"F1.opExtrude","CAP_EDGE",EDGE,{"disambiguationData":[OSD([sQuery(id+"F0.wireOp",EDGE,"E32")])],"isStart":true});
            var Q46;
            Q46=makeQuery(id+"F1.opExtrude","CAP_EDGE",EDGE,{"disambiguationData":[OSD([sQuery(id+"F0.wireOp",EDGE,"E18.top")])],"isStart":true});
            var Q47;
            Q47=makeQuery(id+"F1.opExtrude","CAP_EDGE",EDGE,{"disambiguationData":[OSD([sQuery(id+"F0.wireOp",EDGE,"E9"),sQuery(id+"F0.wireOp",EDGE,"E19.trimOffspring"),sQuery(id+"F0.wireOp",EDGE,"E20.trimOffspring"),sQuery(id+"F0.wireOp",EDGE,"E22"),sQuery(id+"F0.wireOp",EDGE,"E23")])],"isStart":true});
            var Q48;
            Q48=makeQuery(id+"F1.opExtrude","CAP_EDGE",EDGE,{"disambiguationData":[OSD([sQuery(id+"F0.wireOp",EDGE,"E17.right"),sQuery(id+"F0.wireOp",EDGE,"E18.right")])],"isStart":true});
            var Q49;
            Q49=makeQuery(id+"F1.opExtrude","CAP_EDGE",EDGE,{"disambiguationData":[OSD([sQuery(id+"F0.wireOp",EDGE,"E25.top"),sQuery(id+"F0.wireOp",EDGE,"E34")])],"isStart":true});
            var Q50;
            Q50=makeQuery(id+"F1.opExtrude","CAP_EDGE",EDGE,{"disambiguationData":[OSD([sQuery(id+"F0.wireOp",EDGE,"E24.right")])],"isStart":true});
            var Q51;
            Q51=makeQuery(id+"F1.opExtrude","CAP_EDGE",EDGE,{"disambiguationData":[OSD([sQuery(id+"F0.wireOp",EDGE,"E12.trimOffspring"),sQuery(id+"F0.wireOp",EDGE,"E24.bottom")])],"isStart":true});
            var Q52;
            Q52=makeQuery(id+"F1.opExtrude","CAP_EDGE",EDGE,{"disambiguationData":[OSD([sQuery(id+"F0.wireOp",EDGE,"E10.right")])],"isStart":true});
            var Q53;
            Q53=makeQuery(id+"F1.opExtrude","CAP_EDGE",EDGE,{"disambiguationData":[OSD([sQuery(id+"F0.wireOp",EDGE,"E33.top")])],"isStart":true});
            var Q54;
            Q54=makeQuery(id+"F1.opExtrude","SWEPT_EDGE",EDGE,{"disambiguationData":[OSD([sQuery(id+"F0.wireOp",EDGE,"E18.right"),sQuery(id+"F0.wireOp",EDGE,"E33.top")])]});
            chamfer(context, id + "F6", {"entities" : qUnion([Q0, Q1, Q2, Q3, Q4, Q5, Q6, Q7, Q8, Q9, Q10, Q11, Q12, Q13, Q14, Q15, Q16, Q17, Q18, Q19, Q20, Q21, Q22, Q23, Q24, Q25, Q26, Q27, Q28, Q29, Q30, Q31, Q32, Q33, Q34, Q35, Q36, Q37, Q38, Q39, Q40, Q41, Q42, Q43, Q44, Q45, Q46, Q47, Q48, Q49, Q50, Q51, Q52, Q53, Q54]), "width" : .4 * mm, "tangentPropagation" : true});
        }
        {
            var Q0;
            Q0=makeQuery(id+"F1.opExtrude","CAP_FACE",FACE,{"disambiguationData":[OSD([sQuery(id+"F0.wireOp",EDGE,"E0.rect.bottom"),sQuery(id+"F0.wireOp",EDGE,"E0.rect.top"),sQuery(id+"F0.wireOp",EDGE,"E0.rect.left"),sQuery(id+"F0.wireOp",EDGE,"E0.rect.right"),sQuery(id+"F0.wireOp",EDGE,"E1.left"),sQuery(id+"F0.wireOp",EDGE,"E2.bottom"),sQuery(id+"F0.wireOp",EDGE,"E2.left"),sQuery(id+"F0.wireOp",EDGE,"E3.bottom"),sQuery(id+"F0.wireOp",EDGE,"E3.left"),sQuery(id+"F0.wireOp",EDGE,"E4.bottom"),sQuery(id+"F0.wireOp",EDGE,"E4.left"),sQuery(id+"F0.wireOp",EDGE,"E5"),sQuery(id+"F0.wireOp",EDGE,"E6"),sQuery(id+"F0.wireOp",EDGE,"E7"),sQuery(id+"F0.wireOp",EDGE,"E8"),sQuery(id+"F0.wireOp",EDGE,"E9"),sQuery(id+"F0.wireOp",EDGE,"E10.top"),sQuery(id+"F0.wireOp",EDGE,"E10.left"),sQuery(id+"F0.wireOp",EDGE,"E10.right"),sQuery(id+"F0.wireOp",EDGE,"E11.left"),sQuery(id+"F0.wireOp",EDGE,"E11.right"),sQuery(id+"F0.wireOp",EDGE,"E12.trimOffspring"),sQuery(id+"F0.wireOp",EDGE,"E11.top"),sQuery(id+"F0.wireOp",EDGE,"E29.top"),sQuery(id+"F0.wireOp",EDGE,"E29.left"),sQuery(id+"F0.wireOp",EDGE,"E29.right"),sQuery(id+"F0.wireOp",EDGE,"E15.top"),sQuery(id+"F0.wireOp",EDGE,"E13.right"),sQuery(id+"F0.wireOp",EDGE,"E15.right"),sQuery(id+"F0.wireOp",EDGE,"E16"),sQuery(id+"F0.wireOp",EDGE,"E17.left"),sQuery(id+"F0.wireOp",EDGE,"E17.right"),sQuery(id+"F0.wireOp",EDGE,"b61ca566-ba07-4bff-9836-ffdb72489c4c.left"),sQuery(id+"F0.wireOp",EDGE,"b61ca566-ba07-4bff-9836-ffdb72489c4c.right"),sQuery(id+"F0.wireOp",EDGE,"E18.top"),sQuery(id+"F0.wireOp",EDGE,"E18.left"),sQuery(id+"F0.wireOp",EDGE,"E18.right"),sQuery(id+"F0.wireOp",EDGE,"E19.trimOffspring"),sQuery(id+"F0.wireOp",EDGE,"E20.trimOffspring"),sQuery(id+"F0.wireOp",EDGE,"54661143-fa5e-42c1-9d10-70f3552f3fbd"),sQuery(id+"F0.wireOp",EDGE,"E30"),sQuery(id+"F0.wireOp",EDGE,"E22"),sQuery(id+"F0.wireOp",EDGE,"E23")])],"isStart":true});
            chamfer(context, id + "F7", {"entities" : qUnion([Q0]), "width" : .4 * mm, "tangentPropagation" : true});
        }
        {
            var Q0;
            Q0=makeQuery(id+"F1.opExtrude","SWEPT_BODY",BODY,{"disambiguationData":[OSD([sQuery(id+"F0.wireOp",EDGE,"E0.rect.bottom"),sQuery(id+"F0.wireOp",EDGE,"E0.rect.top"),sQuery(id+"F0.wireOp",EDGE,"E0.rect.left"),sQuery(id+"F0.wireOp",EDGE,"E0.rect.right"),sQuery(id+"F0.wireOp",EDGE,"E1.left"),sQuery(id+"F0.wireOp",EDGE,"E2.bottom"),sQuery(id+"F0.wireOp",EDGE,"E2.left"),sQuery(id+"F0.wireOp",EDGE,"E3.bottom"),sQuery(id+"F0.wireOp",EDGE,"E3.left"),sQuery(id+"F0.wireOp",EDGE,"E4.bottom"),sQuery(id+"F0.wireOp",EDGE,"E4.left"),sQuery(id+"F0.wireOp",EDGE,"E5"),sQuery(id+"F0.wireOp",EDGE,"E6"),sQuery(id+"F0.wireOp",EDGE,"E7"),sQuery(id+"F0.wireOp",EDGE,"E8"),sQuery(id+"F0.wireOp",EDGE,"E9"),sQuery(id+"F0.wireOp",EDGE,"E10.top"),sQuery(id+"F0.wireOp",EDGE,"E10.left"),sQuery(id+"F0.wireOp",EDGE,"E10.right"),sQuery(id+"F0.wireOp",EDGE,"E11.left"),sQuery(id+"F0.wireOp",EDGE,"E11.right"),sQuery(id+"F0.wireOp",EDGE,"E12.trimOffspring"),sQuery(id+"F0.wireOp",EDGE,"E11.top"),sQuery(id+"F0.wireOp",EDGE,"E29.top"),sQuery(id+"F0.wireOp",EDGE,"E29.left"),sQuery(id+"F0.wireOp",EDGE,"E29.right"),sQuery(id+"F0.wireOp",EDGE,"E15.top"),sQuery(id+"F0.wireOp",EDGE,"E13.right"),sQuery(id+"F0.wireOp",EDGE,"E15.right"),sQuery(id+"F0.wireOp",EDGE,"E16"),sQuery(id+"F0.wireOp",EDGE,"E17.left"),sQuery(id+"F0.wireOp",EDGE,"E17.right"),sQuery(id+"F0.wireOp",EDGE,"b61ca566-ba07-4bff-9836-ffdb72489c4c.left"),sQuery(id+"F0.wireOp",EDGE,"b61ca566-ba07-4bff-9836-ffdb72489c4c.right"),sQuery(id+"F0.wireOp",EDGE,"E18.top"),sQuery(id+"F0.wireOp",EDGE,"E18.left"),sQuery(id+"F0.wireOp",EDGE,"E18.right"),sQuery(id+"F0.wireOp",EDGE,"E19.trimOffspring"),sQuery(id+"F0.wireOp",EDGE,"E20.trimOffspring"),sQuery(id+"F0.wireOp",EDGE,"54661143-fa5e-42c1-9d10-70f3552f3fbd"),sQuery(id+"F0.wireOp",EDGE,"E30"),sQuery(id+"F0.wireOp",EDGE,"E22"),sQuery(id+"F0.wireOp",EDGE,"E23")])]});
            var Q1;
            {var subQ0=sQuery(id+"F0.wireOp",EDGE,"E0.rect.top");var subQ1=sQuery(id+"F0.wireOp",EDGE,"E2.bottom");var subQ2=sQuery(id+"F0.wireOp",EDGE,"E3.bottom");Q1=makeQuery(id+"F7.opChamfer","BLEND_EDGE",EDGE,{"blendedFrom":[makeQuery(id+"F1.opExtrude","CAP_EDGE",EDGE,{"disambiguationData":[OSD([subQ0,subQ1,subQ2])],"isStart":true}),makeQuery(id+"F1.opExtrude","SWEPT_FACE",FACE,{"disambiguationData":[OSD([subQ0,subQ1,subQ2])]})],"blendedInto":[makeQuery(id+"F1.opExtrude","SWEPT_FACE",FACE,{"disambiguationData":[OSD([subQ0,subQ1,subQ2])]})]});}
            transform(context, id + "F8", {"entities" : qUnion([Q0]), "transformType" : TransformType.ROTATION, "transformAxis" : qUnion([Q1]), "angle" : 180 * degree, "makeCopy" : false});
        }
    });
